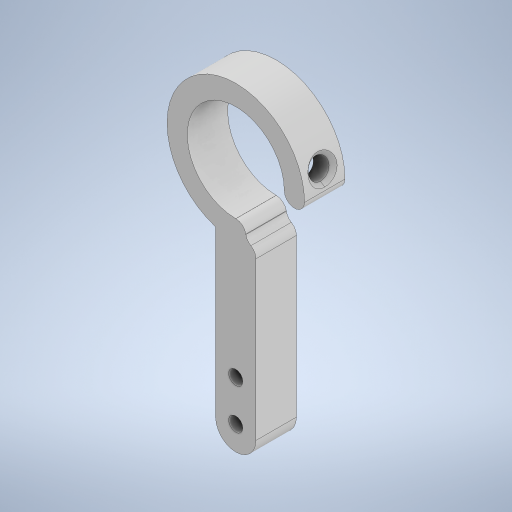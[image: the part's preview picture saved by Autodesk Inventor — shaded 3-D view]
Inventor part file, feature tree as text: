
AUTODESK INVENTOR PART (.ipt)
format: ipt  version: 2023.1 (Build 271208000, 208)  size: 324,096 bytes
history: native  units: mm
features: sketch x4, extrude x3, fillet x2, other x1, revolve x1, chamfer x1
ambient origin geometry x8: Origin, YZ Plane, XZ Plane, XY Plane, X Axis, Y Axis, Z Axis, Center Point
bodies: Body1 (feature_tree)
feature tree (12):
  other  "솔리드1"
  extrude  "돌출1"  Depth=10.0mm
  fillet  "모깎기1"  Radius=50.0mm
  revolve  "회전1"
  chamfer  "모따기1"  Distance=24.0mm
  extrude  "돌출2"  Depth=34.0mm
  fillet  "모깎기2"  Radius=10.0mm
  extrude  "돌출4"  Depth=2.5mm
  sketch  "스케치1"
  sketch  "스케치2"
  sketch  "스케치3"
  sketch  "스케치5"
